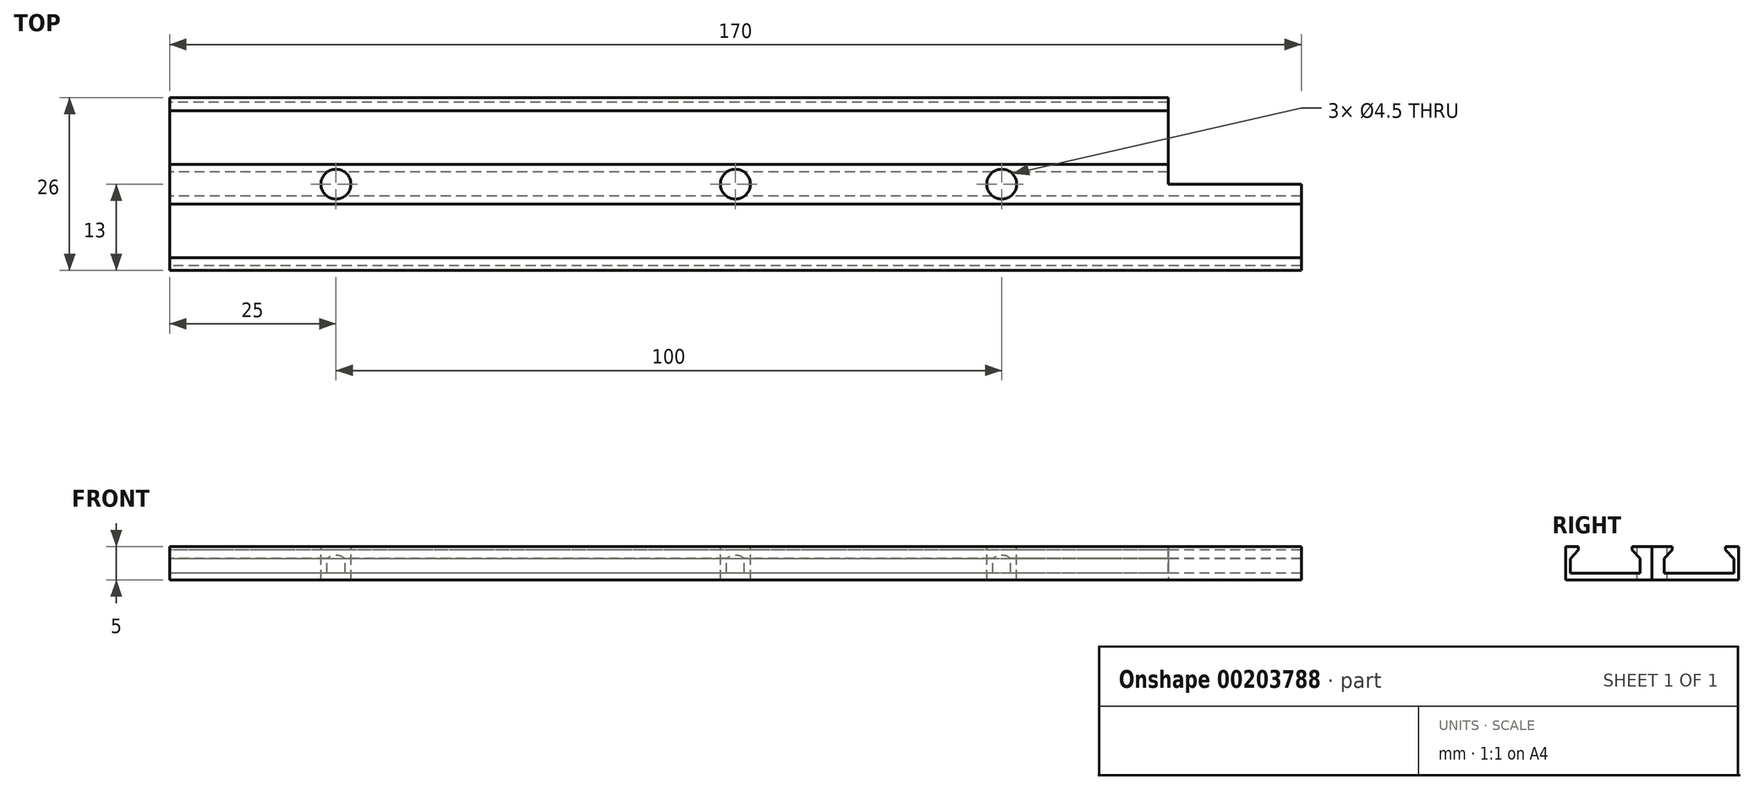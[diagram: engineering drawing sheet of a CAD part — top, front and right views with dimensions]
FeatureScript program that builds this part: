
annotation { "Feature Type Name" : "Feature", "Feature Type Description" : "" }
export const myFeature = defineFeature(function(context is Context, id is Id, definition is map)
    precondition{}
    {
        {
            var Q0;
            Q0=qCreatedBy(makeId("Right.planeOp"),FACE);
            var sketch = newSketch(context, id + "F0", { "sketchPlane" : qUnion([Q0])});
            skLineSegment(sketch, "E0.bottom", {"start": v(13, 2.5) * mm, "end": v(-13, 2.5) * mm});
            skLineSegment(sketch, "E0.top", {"start": v(13, -2.5) * mm, "end": v(-13, -2.5) * mm});
            skLineSegment(sketch, "E0.left", {"start": v(13, 2.5) * mm, "end": v(13, -2.5) * mm});
            skLineSegment(sketch, "E0.right", {"start": v(-13, 2.5) * mm, "end": v(-13, -2.5) * mm});
            skPoint(sketch, "E0.middle", {"position": v(0, 0) * mm});
            skLineSegment(sketch, "E1", {"start": v(0, 0) * mm, "end": v(0, 2.5) * mm, "construction": true});
            skLineSegment(sketch, "E2", {"start": v(0, 2.5) * mm, "end": v(-3, 2.5) * mm, "construction": true});
            skLineSegment(sketch, "E3", {"start": v(-1.8, 0.7) * mm, "end": v(-1.8, -1.5) * mm});
            skLineSegment(sketch, "E4", {"start": v(-1.8, -1.5) * mm, "end": v(-12.3, -1.5) * mm});
            skLineSegment(sketch, "E5", {"start": v(-12.3, -1.5) * mm, "end": v(-12.3, 0.66) * mm});
            skLineSegment(sketch, "E6", {"start": v(-11.05, 2) * mm, "end": v(-11.05, 2.5) * mm});
            skLineSegment(sketch, "E7", {"start": v(-11.05, 2.5) * mm, "end": v(-3, 2.5) * mm});
            skLineSegment(sketch, "E8", {"start": v(-7.03, 2.5) * mm, "end": v(-7.03, -3.55) * mm, "construction": true});
            skLineSegment(sketch, "E9.trimOffspring", {"start": v(-12.3, 0.66) * mm, "end": v(-11.05, 2) * mm});
            skLineSegment(sketch, "E10.MirrorCS", {"start": v(-3, 2) * mm, "end": v(-3, 2.5) * mm});
            skLineSegment(sketch, "E11.MirrorCS", {"start": v(-1.75, 0.66) * mm, "end": v(-3, 2) * mm});
            skLineSegment(sketch, "E12.MirrorCS", {"start": v(3, 2) * mm, "end": v(3, 2.5) * mm});
            skLineSegment(sketch, "E13.MirrorCS", {"start": v(11.05, 2) * mm, "end": v(11.05, 2.5) * mm});
            skLineSegment(sketch, "E14.MirrorCS", {"start": v(1.75, 0.66) * mm, "end": v(3, 2) * mm});
            skLineSegment(sketch, "E15.MirrorCS", {"start": v(12.3, 0.66) * mm, "end": v(11.05, 2) * mm});
            skLineSegment(sketch, "E16.MirrorCS", {"start": v(12.3, -1.5) * mm, "end": v(12.3, 0.66) * mm});
            skLineSegment(sketch, "E17.MirrorCS", {"start": v(1.8, 0.7) * mm, "end": v(1.8, -1.5) * mm});
            skLineSegment(sketch, "E18.MirrorCS", {"start": v(1.8, -1.5) * mm, "end": v(12.3, -1.5) * mm});
            skLineSegment(sketch, "E19.MirrorCS", {"start": v(11.05, 2.5) * mm, "end": v(3, 2.5) * mm});
            skSolve(sketch);
        }
        {
            var Q0;
            Q0=makeQuery(id+"F0.imprint","IMPRINT",FACE,{"disambiguationData":[TD([[makeQuery(id+"F0.imprint","IMPRINT",EDGE,{"derivedFrom":sQuery(id+"F0.wireOp",EDGE,"E0.top")}),-1.0]])]});
            extrude(context, id + "F1", {"entities" : qUnion([Q0]), "depth" : 170 * mm, "symmetric" : true});
        }
        {
            var Q0;
            Q0=makeQuery(id+"F1.opExtrude","SWEPT_FACE",FACE,{"disambiguationData":[OSD([sQuery(id+"F0.wireOp",EDGE,"E0.top")])]});
            var sketch = newSketch(context, id + "F2", { "sketchPlane" : qUnion([Q0])});
            skLineSegment(sketch, "E20", {"start": v(85, -13) * mm, "end": v(85, 0) * mm});
            skLineSegment(sketch, "E21", {"start": v(85, 0) * mm, "end": v(65, 0) * mm});
            skPoint(sketch, "E21.endSnap0", {"position": v(-85, 0) * mm});
            skLineSegment(sketch, "E22", {"start": v(65, 0) * mm, "end": v(65, -13) * mm});
            skLineSegment(sketch, "E23", {"start": v(65, -13) * mm, "end": v(85, -13) * mm});
            skSolve(sketch);
        }
        {
            var Q0;
            Q0=makeQuery(id+"F2.imprint","IMPRINT",FACE,{"disambiguationData":[TD([[makeQuery(id+"F2.imprint","IMPRINT",EDGE,{"derivedFrom":sQuery(id+"F2.wireOp",EDGE,"E20")}),1.0]])]});
            extrude(context, id + "F3", {"entities" : qUnion([Q0]), "operationType" : NewBodyOperationType.REMOVE, "endBound" : BoundingType.UP_TO_NEXT, "oppositeDirection" : true, "depth" : 25 * mm});
        }
        {
            var Q0;
            {var subQ0=sQuery(id+"F0.wireOp",EDGE,"E0.bottom");Q0=makeQuery(id+"F1.opExtrude","SWEPT_FACE",FACE,{"disambiguationData":[OSD([subQ0]),TDD([makeQuery(id+"F0.imprint","IMPRINT",EDGE,{"disambiguationData":[TD([[makeQuery(id+"F0.imprint","INTERSECT",VERTEX,{"derivedFrom":[subQ0,sQuery(id+"F0.wireOp",EDGE,"E7"),sQuery(id+"F0.wireOp",EDGE,"E10.MirrorCS")]}),1.0]])],"derivedFrom":subQ0})])]});}
            var sketch = newSketch(context, id + "F4", { "sketchPlane" : qUnion([Q0])});
            skLineSegment(sketch, "E24", {"start": v(0, 0) * mm, "end": v(-60, 0) * mm, "construction": true});
            skPoint(sketch, "E24.endSnap0", {"position": v(-85, 0) * mm});
            skLineSegment(sketch, "E25", {"start": v(0, 0) * mm, "end": v(40, 0) * mm, "construction": true});
            skCircle(sketch, "E26", {"center": v(-60, 0) * mm, "radius": 2.25 * mm});
            skCircle(sketch, "E27", {"center": v(0, 0) * mm, "radius": 2.25 * mm});
            skCircle(sketch, "E28", {"center": v(40, 0) * mm, "radius": 2.25 * mm});
            skSolve(sketch);
        }
        {
            var Q0;
            Q0=makeQuery(id+"F4.imprint","IMPRINT",FACE,{"disambiguationData":[TD([[makeQuery(id+"F4.imprint","IMPRINT",EDGE,{"derivedFrom":sQuery(id+"F4.wireOp",EDGE,"E26")}),1.0]])]});
            var Q1;
            Q1=makeQuery(id+"F4.imprint","IMPRINT",FACE,{"disambiguationData":[TD([[makeQuery(id+"F4.imprint","IMPRINT",EDGE,{"derivedFrom":sQuery(id+"F4.wireOp",EDGE,"E27")}),1.0]])]});
            var Q2;
            Q2=makeQuery(id+"F4.imprint","IMPRINT",FACE,{"disambiguationData":[TD([[makeQuery(id+"F4.imprint","IMPRINT",EDGE,{"derivedFrom":sQuery(id+"F4.wireOp",EDGE,"E28")}),1.0]])]});
            extrude(context, id + "F5", {"entities" : qUnion([Q0, Q1, Q2]), "operationType" : NewBodyOperationType.REMOVE, "endBound" : BoundingType.UP_TO_NEXT, "oppositeDirection" : true, "depth" : 25 * mm});
        }
    });
